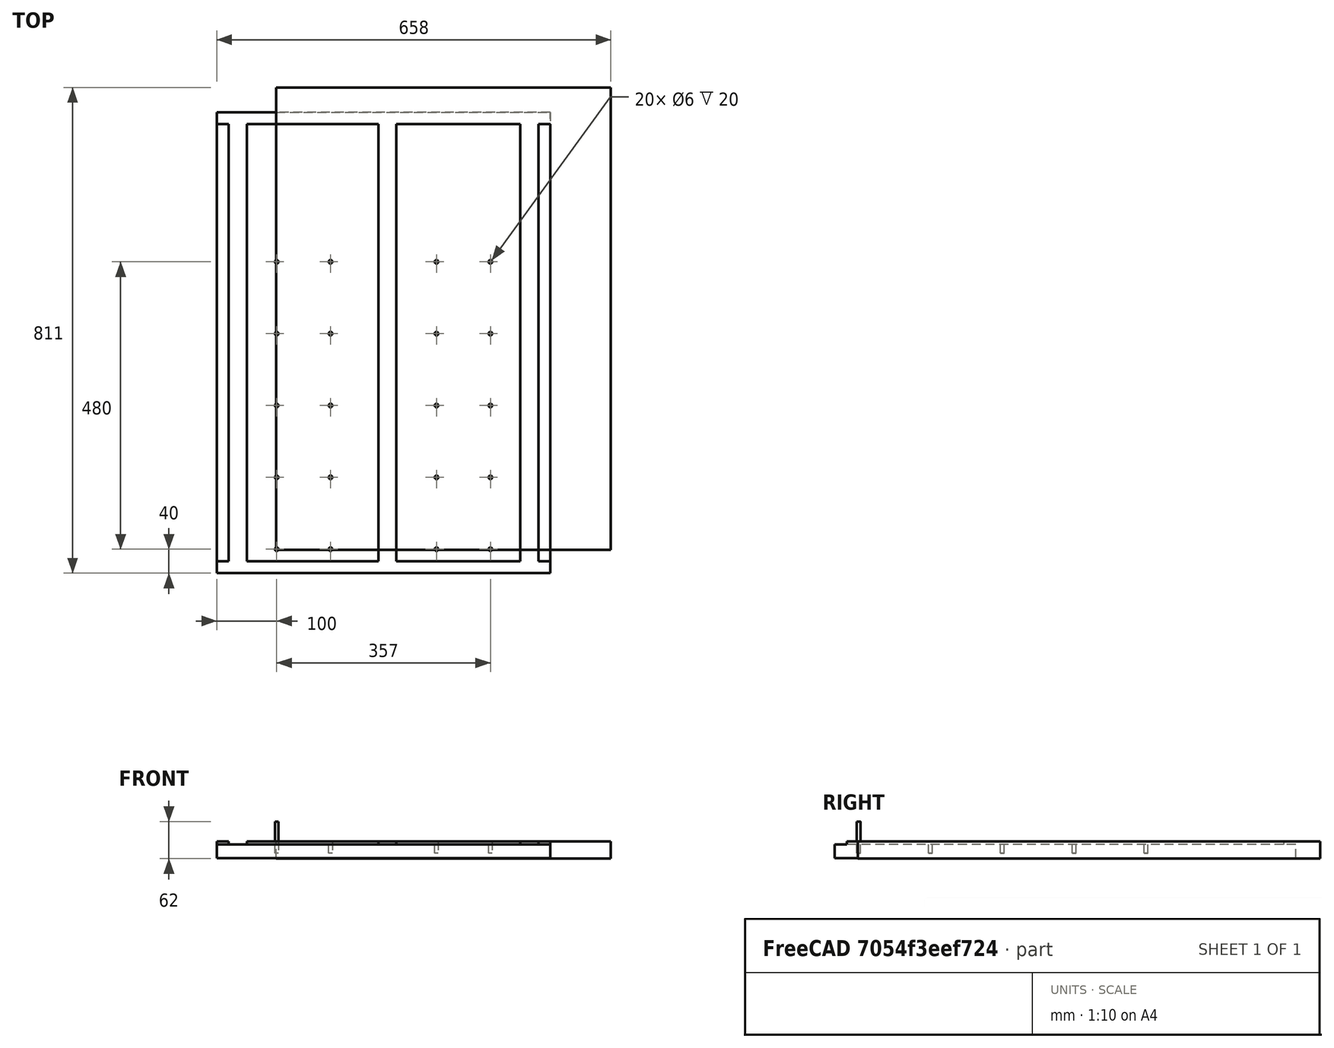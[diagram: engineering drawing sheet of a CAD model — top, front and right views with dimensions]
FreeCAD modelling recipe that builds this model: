
FCSTD DOCUMENT  (FreeCAD 0.19R24267 (Git))
Label: holy-dowels
License: All rights reserved
LicenseURL: http://en.wikipedia.org/wiki/All_rights_reserved
objects: Sketcher::SketchObject×3, Part::FeaturePython×3, Path::FeaturePython×3, PartDesign::Pocket×2, App::DocumentObjectGroup×2, Mesh::FeaturePython×2, PartDesign::Pad×1, PartDesign::Body×1, App::FeaturePython×1, Path::FeatureCompoundPython×1
note: 13 computed .brp shape members not serialized (recipe doc carries the construction recipe); baked Part::Feature solids carry a one-line shape summary decoded from their .brp

FEATURE [Sketcher::SketchObject] Sketch
  FullyConstrained = true
  MapMode = 5
  Support = -> [XY_Plane]
  sketch-geometry (4):
    g0: LineSegment StartX=0 StartY=0 StartZ=0 EndX=557 EndY=0 EndZ=0
    g1: LineSegment StartX=557 StartY=0 StartZ=0 EndX=557 EndY=770 EndZ=0
    g2: LineSegment StartX=557 StartY=770 StartZ=0 EndX=0 EndY=770 EndZ=0
    g3: LineSegment StartX=0 StartY=770 StartZ=0 EndX=0 EndY=0 EndZ=0
  constraints (11):
    c: Coincident(g0,g1)
    c: Coincident(g1,g2)
    c: Coincident(g2,g3)
    c: Coincident(g3,g0)
    c: Horizontal(g0)
    c: Horizontal(g2)
    c: Vertical(g1)
    c: Vertical(g3)
    c: Distance(g3) = 770
    c: Distance(g2) = 557
    c: Coincident(g-1,g0)
FEATURE [PartDesign::Pad] Pad  label="Board"
  Direction = (1,1,1)
  Length = 28
  Length2 = 100
  Profile = -> Sketch
  Type = 0
FEATURE [Sketcher::SketchObject] Sketch001
  ExternalGeometry = -> [Pad]
  FullyConstrained = true
  MapMode = 5
  Placement = pos=(0,0,28) rot=(0,0,1;0rad)
  Support = -> [Pad]
  sketch-geometry (26):
    g0: LineSegment StartX=0 StartY=770 StartZ=0 EndX=557 EndY=770 EndZ=0
    g1: LineSegment StartX=557 StartY=770 StartZ=0 EndX=557 EndY=750 EndZ=0
    g2: LineSegment StartX=557 StartY=750 StartZ=0 EndX=537 EndY=750 EndZ=0
    g3: LineSegment StartX=537 StartY=750 StartZ=0 EndX=537 EndY=20 EndZ=0
    g4: LineSegment StartX=537 StartY=20 StartZ=0 EndX=557 EndY=20 EndZ=0
    g5: LineSegment StartX=557 StartY=20 StartZ=0 EndX=557 EndY=0 EndZ=0
    g6: LineSegment StartX=557 StartY=0 StartZ=0 EndX=0 EndY=0 EndZ=0
    g7: LineSegment StartX=0 StartY=0 StartZ=0 EndX=0 EndY=20 EndZ=0
    g8: LineSegment StartX=0 StartY=20 StartZ=0 EndX=20 EndY=20 EndZ=0
    g9: LineSegment StartX=20 StartY=20 StartZ=0 EndX=20 EndY=750 EndZ=0
    g10: LineSegment StartX=20 StartY=750 StartZ=0 EndX=0 EndY=750 EndZ=0
    g11: LineSegment StartX=0 StartY=750 StartZ=0 EndX=0 EndY=770 EndZ=0
    g12: LineSegment StartX=50 StartY=750 StartZ=0 EndX=270 EndY=750 EndZ=0
    g13: LineSegment StartX=270 StartY=750 StartZ=0 EndX=270 EndY=20 EndZ=0
    g14: LineSegment StartX=270 StartY=20 StartZ=0 EndX=50 EndY=20 EndZ=0
    g15: LineSegment StartX=50 StartY=20 StartZ=0 EndX=50 EndY=750 EndZ=0
    g16: LineSegment StartX=300 StartY=750 StartZ=0 EndX=507 EndY=750 EndZ=0
    g17: LineSegment StartX=507 StartY=750 StartZ=0 EndX=507 EndY=20 EndZ=0
    g18: LineSegment StartX=507 StartY=20 StartZ=0 EndX=300 EndY=20 EndZ=0
    g19: LineSegment StartX=300 StartY=20 StartZ=0 EndX=300 EndY=750 EndZ=0
    g20: LineSegment StartX=20 StartY=20 StartZ=0 EndX=50 EndY=20 EndZ=0
    g21: LineSegment StartX=270 StartY=20 StartZ=0 EndX=300 EndY=20 EndZ=0
    g22: LineSegment StartX=507 StartY=20 StartZ=0 EndX=537 EndY=20 EndZ=0
    g23: LineSegment StartX=20 StartY=750 StartZ=0 EndX=50 EndY=750 EndZ=0
    g24: LineSegment StartX=270 StartY=750 StartZ=0 EndX=300 EndY=750 EndZ=0
    g25: LineSegment StartX=507 StartY=750 StartZ=0 EndX=537 EndY=750 EndZ=0
  constraints (68):
    c: Coincident(g0,g1)
    c: Coincident(g1,g2)
    c: Coincident(g2,g3)
    c: Coincident(g3,g4)
    c: Coincident(g4,g5)
    c: Coincident(g5,g6)
    c: Coincident(g6,g7)
    c: Coincident(g7,g8)
    c: Coincident(g8,g9)
    c: Coincident(g9,g10)
    c: Coincident(g10,g11)
    c: Coincident(g11,g0)
    c: Distance(g5) = 20
    c: Distance(g4) = 20
    c: Coincident(g5,g-5)
    c: Coincident(g-1,g6)
    c: Coincident(g0,g-3)
    c: Coincident(g0,g-5)
    c: Coincident(g12,g13)
    c: Coincident(g13,g14)
    c: Coincident(g14,g15)
    c: Coincident(g15,g12)
    c: Coincident(g16,g17)
    c: Coincident(g17,g18)
    c: Coincident(g18,g19)
    c: Coincident(g19,g16)
    c: Coincident(g20,g8)
    c: Coincident(g20,g14)
    c: Coincident(g21,g13)
    c: Coincident(g21,g18)
    c: Coincident(g22,g17)
    c: Coincident(g22,g3)
    c: Coincident(g25,g2)
    c: Coincident(g25,g16)
    c: Coincident(g16,g24)
    c: Coincident(g24,g12)
    c: Coincident(g12,g23)
    c: Coincident(g23,g9)
    c: Distance(g20) = 30
    c: Distance(g21) = 30
    c: Distance(g22) = 30
    c: Distance(g1) = 20
    c: Vertical(g7)
    c: Vertical(g11)
    c: Vertical(g1)
    c: Vertical(g5)
    c: Horizontal(g22)
    c: Horizontal(g21)
    c: Horizontal(g20)
    c: Horizontal(g8)
    c: Horizontal(g14)
    c: Horizontal(g18)
    c: Horizontal(g4)
    c: Horizontal(g10)
    c: Horizontal(g23)
    c: Horizontal(g12)
    c: Horizontal(g24)
    c: Horizontal(g16)
    c: Horizontal(g25)
    c: Horizontal(g2)
    c: Vertical(g9)
    c: Vertical(g15)
    c: Vertical(g13)
    c: Vertical(g19)
    c: Vertical(g17)
    c: Vertical(g3)
    c: Distance(g8) = 20
    c: Distance(g14) = 220
FEATURE [PartDesign::Pocket] Pocket  label="Frame Outline"
  BaseFeature = -> Pad
  Length = 5
  Length2 = 100
  Profile = -> Sketch001
  Type = 0
FEATURE [Sketcher::SketchObject] Sketch002
  ExternalGeometry = -> [Pad]
  FullyConstrained = true
  MapMode = 5
  Placement = pos=(0,0,28) rot=(0,0,1;0rad)
  Support = -> [Pad]
  sketch-geometry (50):
    g0: LineSegment StartX=0 StartY=40 StartZ=0 EndX=100 EndY=40 EndZ=0
    g1: LineSegment StartX=100 StartY=40 StartZ=0 EndX=190 EndY=40 EndZ=0
    g2: LineSegment StartX=190 StartY=40 StartZ=0 EndX=367 EndY=40 EndZ=0
    g3: LineSegment StartX=367 StartY=40 StartZ=0 EndX=457 EndY=40 EndZ=0
    g4: LineSegment StartX=457 StartY=40 StartZ=0 EndX=557 EndY=40 EndZ=0
    g5: Circle CenterX=100 CenterY=40 CenterZ=0 NormalX=0 NormalY=0 NormalZ=1 AngleXU=0 Radius=3
    g6: Circle CenterX=190 CenterY=40 CenterZ=0 NormalX=0 NormalY=0 NormalZ=1 AngleXU=0 Radius=3
    g7: Circle CenterX=367 CenterY=40 CenterZ=0 NormalX=0 NormalY=0 NormalZ=1 AngleXU=0 Radius=3
    g8: Circle CenterX=457 CenterY=40 CenterZ=0 NormalX=0 NormalY=0 NormalZ=1 AngleXU=0 Radius=3
    g9: LineSegment StartX=0 StartY=40 StartZ=0 EndX=0 EndY=0 EndZ=0
    g10: LineSegment StartX=0 StartY=160 StartZ=0 EndX=100 EndY=160 EndZ=0
    g11: LineSegment StartX=100 StartY=160 StartZ=0 EndX=190 EndY=160 EndZ=0
    g12: LineSegment StartX=190 StartY=160 StartZ=0 EndX=367 EndY=160 EndZ=0
    g13: LineSegment StartX=367 StartY=160 StartZ=0 EndX=457 EndY=160 EndZ=0
    g14: LineSegment StartX=457 StartY=160 StartZ=0 EndX=557 EndY=160 EndZ=0
    g15: LineSegment StartX=557 StartY=280 StartZ=0 EndX=457 EndY=280 EndZ=0
    g16: LineSegment StartX=457 StartY=280 StartZ=0 EndX=367 EndY=280 EndZ=0
    g17: LineSegment StartX=367 StartY=280 StartZ=0 EndX=190 EndY=280 EndZ=0
    g18: LineSegment StartX=190 StartY=280 StartZ=0 EndX=100 EndY=280 EndZ=0
    g19: LineSegment StartX=100 StartY=280 StartZ=0 EndX=0 EndY=280 EndZ=0
    g20: LineSegment StartX=0 StartY=400 StartZ=0 EndX=100 EndY=400 EndZ=0
    g21: LineSegment StartX=100 StartY=400 StartZ=0 EndX=190 EndY=400 EndZ=0
    g22: LineSegment StartX=190 StartY=400 StartZ=0 EndX=367 EndY=400 EndZ=0
    g23: LineSegment StartX=367 StartY=400 StartZ=0 EndX=457 EndY=400 EndZ=0
    g24: LineSegment StartX=457 StartY=400 StartZ=0 EndX=557 EndY=400 EndZ=0
    g25: LineSegment StartX=557 StartY=520 StartZ=0 EndX=457 EndY=520 EndZ=0
    g26: LineSegment StartX=457 StartY=520 StartZ=0 EndX=367 EndY=520 EndZ=0
    g27: LineSegment StartX=367 StartY=520 StartZ=0 EndX=190 EndY=520 EndZ=0
    g28: LineSegment StartX=190 StartY=520 StartZ=0 EndX=100 EndY=520 EndZ=0
    g29: LineSegment StartX=100 StartY=520 StartZ=0 EndX=0 EndY=520 EndZ=0
    g30: LineSegment StartX=0 StartY=520 StartZ=0 EndX=0 EndY=400 EndZ=0
    g31: LineSegment StartX=0 StartY=400 StartZ=0 EndX=0 EndY=280 EndZ=0
    g32: LineSegment StartX=0 StartY=280 StartZ=0 EndX=0 EndY=160 EndZ=0
    g33: LineSegment StartX=0 StartY=160 StartZ=0 EndX=0 EndY=40 EndZ=0
    g34: Circle CenterX=100 CenterY=160 CenterZ=0 NormalX=0 NormalY=0 NormalZ=1 AngleXU=0 Radius=3
    g35: Circle CenterX=190 CenterY=160 CenterZ=0 NormalX=0 NormalY=0 NormalZ=1 AngleXU=0 Radius=3
    g36: Circle CenterX=367 CenterY=160 CenterZ=0 NormalX=0 NormalY=0 NormalZ=1 AngleXU=0 Radius=3
    g37: Circle CenterX=457 CenterY=160 CenterZ=0 NormalX=0 NormalY=0 NormalZ=1 AngleXU=0 Radius=3
    g38: Circle CenterX=100 CenterY=280 CenterZ=0 NormalX=0 NormalY=0 NormalZ=1 AngleXU=0 Radius=3
    g39: Circle CenterX=190 CenterY=280 CenterZ=0 NormalX=0 NormalY=0 NormalZ=1 AngleXU=0 Radius=3
    g40: Circle CenterX=367 CenterY=280 CenterZ=0 NormalX=0 NormalY=0 NormalZ=1 AngleXU=0 Radius=3
    g41: Circle CenterX=457 CenterY=280 CenterZ=0 NormalX=0 NormalY=0 NormalZ=1 AngleXU=0 Radius=3
    g42: Circle CenterX=100 CenterY=400 CenterZ=0 NormalX=0 NormalY=0 NormalZ=1 AngleXU=0 Radius=3
    g43: Circle CenterX=190 CenterY=400 CenterZ=0 NormalX=0 NormalY=0 NormalZ=1 AngleXU=0 Radius=3
    g44: Circle CenterX=367 CenterY=400 CenterZ=0 NormalX=0 NormalY=0 NormalZ=1 AngleXU=0 Radius=3
    g45: Circle CenterX=457 CenterY=400 CenterZ=0 NormalX=0 NormalY=0 NormalZ=1 AngleXU=0 Radius=3
    g46: Circle CenterX=100 CenterY=520 CenterZ=0 NormalX=0 NormalY=0 NormalZ=1 AngleXU=0 Radius=3
    g47: Circle CenterX=190 CenterY=520 CenterZ=0 NormalX=0 NormalY=0 NormalZ=1 AngleXU=0 Radius=3
    g48: Circle CenterX=367 CenterY=520 CenterZ=0 NormalX=0 NormalY=0 NormalZ=1 AngleXU=0 Radius=3
    g49: Circle CenterX=457 CenterY=520 CenterZ=0 NormalX=0 NormalY=0 NormalZ=1 AngleXU=0 Radius=3
  constraints (130):
    c: Horizontal(g0)
    c: Horizontal(g2)
    c: Horizontal(g1)
    c: Horizontal(g4)
    c: Horizontal(g3)
    c: Coincident(g0,g1)
    c: Coincident(g1,g2)
    c: Coincident(g2,g3)
    c: Coincident(g3,g4)
    c: Equal(g8,g7)
    c: Equal(g7,g6)
    c: Equal(g6,g5)
    c: Diameter(g5) = 6
    c: Coincident(g5,g0)
    c: Coincident(g6,g1)
    c: Coincident(g7,g2)
    c: Coincident(g8,g3)
    c: Coincident(g9,g0)
    c: Coincident(g9,g-1)
    c: Vertical(g9)
    c: Distance(g9) = 40
    c: Equal(g0,g4)
    c: Distance(g0) = 100
    c: Equal(g3,g1)
    c: Distance(g1) = 90
    c: PointOnObject(g4,g-4)
    c: Horizontal(g10)
    c: Coincident(g10,g11)
    c: Horizontal(g11)
    c: Coincident(g11,g12)
    c: Horizontal(g12)
    c: Coincident(g12,g13)
    c: Horizontal(g13)
    c: Coincident(g13,g14)
    c: Horizontal(g14)
    c: Coincident(g15,g16)
    c: Coincident(g16,g17)
    c: Horizontal(g17)
    c: Coincident(g17,g18)
    c: Horizontal(g18)
    c: Coincident(g18,g19)
    c: Horizontal(g20)
    c: Coincident(g20,g21)
    c: Coincident(g21,g22)
    c: Coincident(g22,g23)
    c: Coincident(g23,g24)
    c: Horizontal(g24)
    c: Horizontal(g25)
    c: Coincident(g25,g26)
    c: Horizontal(g26)
    c: Coincident(g26,g27)
    c: Horizontal(g27)
    c: Coincident(g27,g28)
    c: Horizontal(g28)
    c: Coincident(g28,g29)
    c: Horizontal(g29)
    c: Horizontal(g21)
    c: Horizontal(g22)
    c: Horizontal(g23)
    c: Horizontal(g15)
    c: Horizontal(g16)
    c: Horizontal(g19)
    c: PointOnObject(g29,g-2)
    c: PointOnObject(g20,g-2)
    c: PointOnObject(g19,g-2)
    c: PointOnObject(g10,g-2)
    c: PointOnObject(g14,g-4)
    c: PointOnObject(g15,g-4)
    c: PointOnObject(g24,g-4)
    c: PointOnObject(g25,g-4)
    c: Equal(g0,g10)
    c: Equal(g10,g19)
    c: Equal(g19,g20)
    c: Equal(g20,g29)
    c: Equal(g4,g14)
    c: Equal(g14,g15)
    c: Equal(g15,g24)
    c: Equal(g24,g25)
    c: Equal(g26,g23)
    c: Equal(g23,g16)
    c: Equal(g16,g13)
    c: Equal(g13,g3)
    c: Equal(g1,g11)
    c: Equal(g11,g18)
    c: Equal(g18,g21)
    c: Equal(g21,g28)
    c: Coincident(g30,g31)
    c: Coincident(g31,g32)
    c: Coincident(g32,g33)
    c: Coincident(g0,g33)
    c: Coincident(g10,g32)
    c: Coincident(g19,g31)
    c: Coincident(g20,g30)
    c: Coincident(g29,g30)
    c: Equal(g30,g31)
    c: Equal(g31,g32)
    c: Equal(g32,g33)
    c: Distance(g33) = 120
    c: Equal(g38,g39)
    c: Equal(g39,g40)
    c: Equal(g40,g41)
    c: Equal(g41,g45)
    c: Equal(g45,g49)
    c: Equal(g49,g48)
    c: Equal(g48,g47)
    c: Equal(g47,g46)
    c: Equal(g46,g42)
    c: Equal(g42,g43)
    c: Equal(g43,g44)
    c: Equal(g44,g34)
    c: Equal(g34,g35)
    c: Equal(g35,g36)
    c: Equal(g36,g37)
    c: Equal(g37,g5)
    c: Coincident(g37,g13)
    c: Coincident(g36,g12)
    c: Coincident(g34,g10)
    c: Coincident(g35,g11)
    c: Coincident(g38,g18)
    c: Coincident(g39,g17)
    c: Coincident(g40,g16)
    c: Coincident(g41,g15)
    c: Coincident(g46,g28)
    c: Coincident(g47,g27)
    c: Coincident(g42,g20)
    c: Coincident(g43,g21)
    c: Coincident(g44,g22)
    c: Coincident(g45,g23)
    c: Coincident(g49,g25)
    c: Coincident(g48,g26)
FEATURE [PartDesign::Pocket] Pocket001  label="Holes"
  BaseFeature = -> Pocket
  Length = 20
  Length2 = 100
  Profile = -> Sketch002
  Type = 0
FEATURE [PartDesign::Body] Body  label="Wastboard"
  Group = -> [Sketch,Pad,Sketch001,Pocket,Sketch002,Pocket001]
  Origin = -> Origin
  Tip = -> Pocket001
FEATURE [App::FeaturePython] SetupSheet  # Path/CAM operation (typed FeaturePython)
  ClearanceHeightExpression = OpStockZMax+SetupSheet.ClearanceHeightOffset
  ClearanceHeightOffset = 5
  CoolantMode = 0
  CoolantModes = None | Flood | Mist
  FinalDepthExpression = OpFinalDepth
  HorizRapid = 0
  SafeHeightExpression = OpStockZMax+SetupSheet.SafeHeightOffset
  SafeHeightOffset = 3
  StartDepthExpression = OpStartDepth
  StepDownExpression = OpToolDiameter
  VertRapid = 0
FEATURE [Part::FeaturePython] Clone  label="Model-Wastboard"  # Draft clone (typed FeaturePython)
  AttacherType = Attacher::AttachEngine3D
  Fuse = false
  Objects = -> [Body]
  PathResource = Model
  Placement = pos=(-100,-40,-28) rot=(0,0,1;0rad)
  Scale = (1,1,1)
FEATURE [App::DocumentObjectGroup] Model
  Group = -> [Clone]
FEATURE [Part::FeaturePython] Stock  # WARN: FeaturePython — macro-defined, semantics opaque (R4)
  Base = -> Model
  ExtXneg = 1
  ExtXpos = 1
  ExtYneg = 1
  ExtYpos = 1
  ExtZneg = 1
  ExtZpos = 0
  Placement = pos=(0,0,-28) rot=(0,0,1;0rad)
  StockType = FromBase
FEATURE [Part::FeaturePython] ToolBit001  label="claas_6mm_endmill"  # Path/CAM toolbit (typed FeaturePython)
  BitPropertyNames = Chipload | CuttingEdgeHeight | Diameter | Flutes | Length | Material | ShankDiameter
  BitShape = <userpath>/Downloads/FreeCAD_0.19.24267_Win-LPv12.5.1_vc17.x-x86-64/Mod/Path/Tools/Shape/endmill.fcstd
  Chipload = 0
  CuttingEdgeHeight = 15
  Diameter = 6
  File = <userpath>/Downloads/bits/Bit/claas_6mm.fctb
  Flutes = 0
  Length = 33
  Material = 0
  ShankDiameter = 6
  ShapeName = endmill
FEATURE [Path::FeaturePython] claas_6mm_endmill  label="claas_6mm_endmill001"  # Path/CAM operation (typed FeaturePython)
  HorizFeed = 5
  HorizRapid = 0
  SpindleDir = 0
  SpindleSpeed = 0
  Tool = -> ToolBit001
  ToolNumber = 1
  VertFeed = 6
  VertRapid = 0
  expr: HorizRapid = SetupSheet.HorizRapid
  expr: VertRapid = SetupSheet.VertRapid
FEATURE [App::DocumentObjectGroup] Tools
  Group = -> [claas_6mm_endmill]
FEATURE [Mesh::FeaturePython] CutMaterial  # WARN: FeaturePython — macro-defined, semantics opaque (R4)
FEATURE [Path::FeaturePython] Drilling  # Path/CAM operation (typed FeaturePython)
  Active = true
  AddTipLength = false
  AttemptInverseAngle = false
  Base = -> [Clone]
  ClearanceHeight = 5
  CoolantMode = None
  CycleTime = 00:01:17
  DwellEnabled = false
  DwellTime = 1
  EnableRotation = 0
  ExtraOffset = 0
  FinalDepth = -20
  InverseAngle = false
  OpFinalDepth = -20
  OpStartDepth = 0
  OpStockZMax = 0
  OpStockZMin = -29
  OpToolDiameter = 6
  PeckDepth = 4.5
  PeckEnabled = false
  RetractHeight = 1
  ReturnLevel = 0
  ReverseDirection = false
  SafeHeight = 3
  StartDepth = 0
  ToolController = -> claas_6mm_endmill
  expr: PeckDepth = OpToolDiameter * 0.75
  expr: ClearanceHeight = OpStockZMax + SetupSheet.ClearanceHeightOffset
  expr: RetractHeight = OpStartDepth + 1mm
  expr: SafeHeight = OpStockZMax + SetupSheet.SafeHeightOffset
  expr: FinalDepth = -20mm
  expr: StartDepth = OpStartDepth
FEATURE [Path::FeatureCompoundPython] Operations  # Path/CAM operation (typed FeaturePython)
  Group = -> [Drilling]
  UsePlacements = false
FEATURE [Path::FeaturePython] Job  # Path/CAM operation (typed FeaturePython)
  CycleTime = 00:01:17
  Fixtures = G54
  GeometryTolerance = 0.01
  LastPostProcessDate = 2021-03-25 17:44:43.942916
  LastPostProcessOutput = <userpath>/git/cnc-projects/holy-dowels/holy-dowels.gcode
  Model = -> Model
  Operations = -> Operations
  OrderOutputBy = 0
  PostProcessor = 5
  PostProcessorArgs = --translate_drill
  PostProcessorOutputFile = holy-dowels.gcode
  SetupSheet = -> SetupSheet
  SplitOutput = false
  Stock = -> Stock
  Tools = -> Tools
FEATURE [Mesh::FeaturePython] CutMaterial001  # WARN: FeaturePython — macro-defined, semantics opaque (R4)
